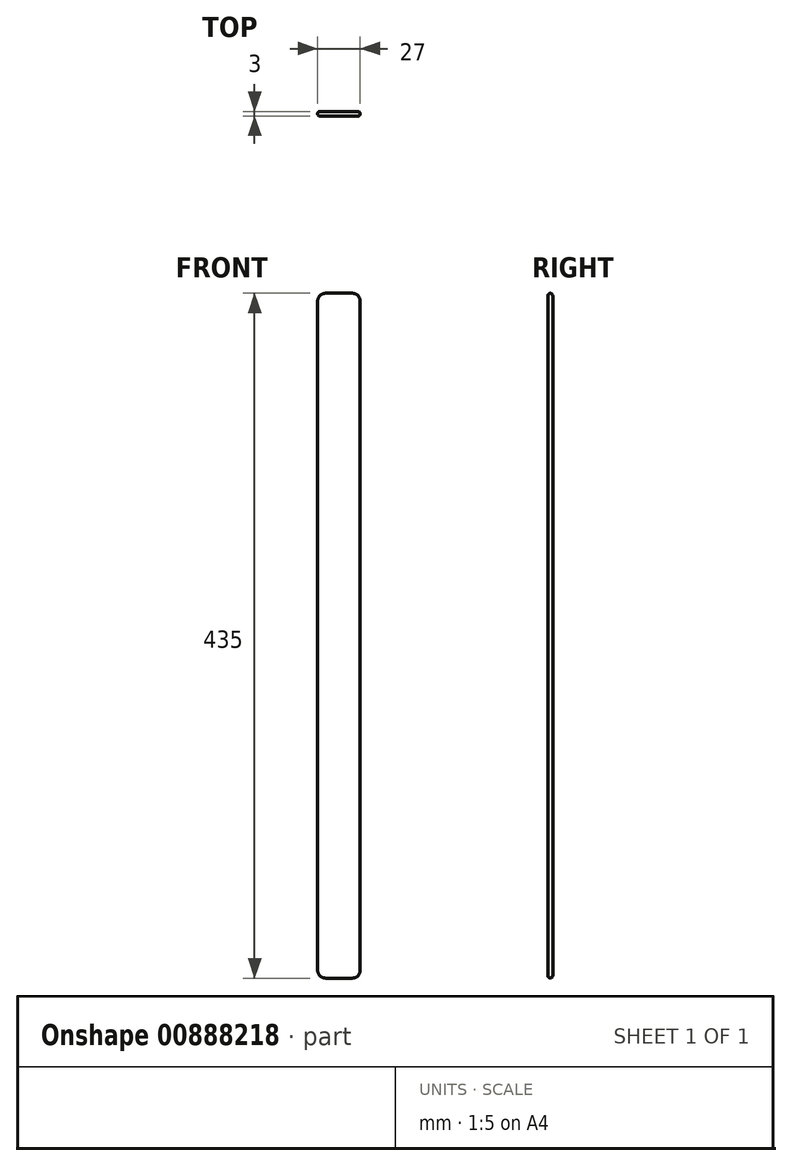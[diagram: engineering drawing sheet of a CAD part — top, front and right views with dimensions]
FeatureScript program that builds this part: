
annotation { "Feature Type Name" : "Feature", "Feature Type Description" : "" }
export const myFeature = defineFeature(function(context is Context, id is Id, definition is map)
    precondition{}
    {
        {
            var Q0;
            Q0=qCreatedBy(makeId("Front.planeOp"),FACE);
            var sketch = newSketch(context, id + "F0", { "sketchPlane" : qUnion([Q0])});
            skLineSegment(sketch, "E0.bottom", {"start": v(8.5, 217.5) * mm, "end": v(-8.5, 217.5) * mm});
            skLineSegment(sketch, "E0.top", {"start": v(8.5, -217.5) * mm, "end": v(-8.5, -217.5) * mm});
            skLineSegment(sketch, "E0.left", {"start": v(13.5, 212.5) * mm, "end": v(13.5, -212.5) * mm});
            skLineSegment(sketch, "E0.right", {"start": v(-13.5, 212.5) * mm, "end": v(-13.5, -212.5) * mm});
            skPoint(sketch, "E0.middle", {"position": v(0, 0) * mm});
            skPoint(sketch, "E1.visualSharp", {"position": v(13.5, 217.5) * mm});
            skArc(sketch, "E1.filletArc", {"start": v(13.5, 212.5) * mm, "mid": v(12.04, 216.04) * mm, "end": v(8.5, 217.5) * mm});
            skPoint(sketch, "E2.visualSharp", {"position": v(-13.5, 217.5) * mm});
            skArc(sketch, "E2.filletArc", {"start": v(-8.5, 217.5) * mm, "mid": v(-12.04, 216.04) * mm, "end": v(-13.5, 212.5) * mm});
            skPoint(sketch, "E3.visualSharp", {"position": v(13.5, -217.5) * mm});
            skArc(sketch, "E3.filletArc", {"start": v(8.5, -217.5) * mm, "mid": v(12.04, -216.04) * mm, "end": v(13.5, -212.5) * mm});
            skPoint(sketch, "E4.visualSharp", {"position": v(-13.5, -217.5) * mm});
            skArc(sketch, "E4.filletArc", {"start": v(-13.5, -212.5) * mm, "mid": v(-12.04, -216.04) * mm, "end": v(-8.5, -217.5) * mm});
            skSolve(sketch);
        }
        {
            var Q0;
            Q0 = qSketchRegion(id + "F0", true);
            extrude(context, id + "F1", {"entities" : qUnion([Q0]), "oppositeDirection" : true, "depth" : 3 * mm, "offsetDistance" : 25 * mm});
        }
        {
            var Q0;
            Q0=makeQuery(id+"F1.opExtrude","CAP_EDGE",EDGE,{"disambiguationData":[OSD([sQuery(id+"F0.wireOp",EDGE,"E0.left")])],"isStart":true});
            var Q1;
            Q1=makeQuery(id+"F1.opExtrude","CAP_EDGE",EDGE,{"disambiguationData":[OSD([sQuery(id+"F0.wireOp",EDGE,"E0.left")])],"isStart":false});
            fillet(context, id + "F2", {"entities" : qUnion([Q0, Q1]), "radius" : 1.5 * mm, "tangentPropagation" : true, "allowEdgeOverflow" : false});
        }
    });
